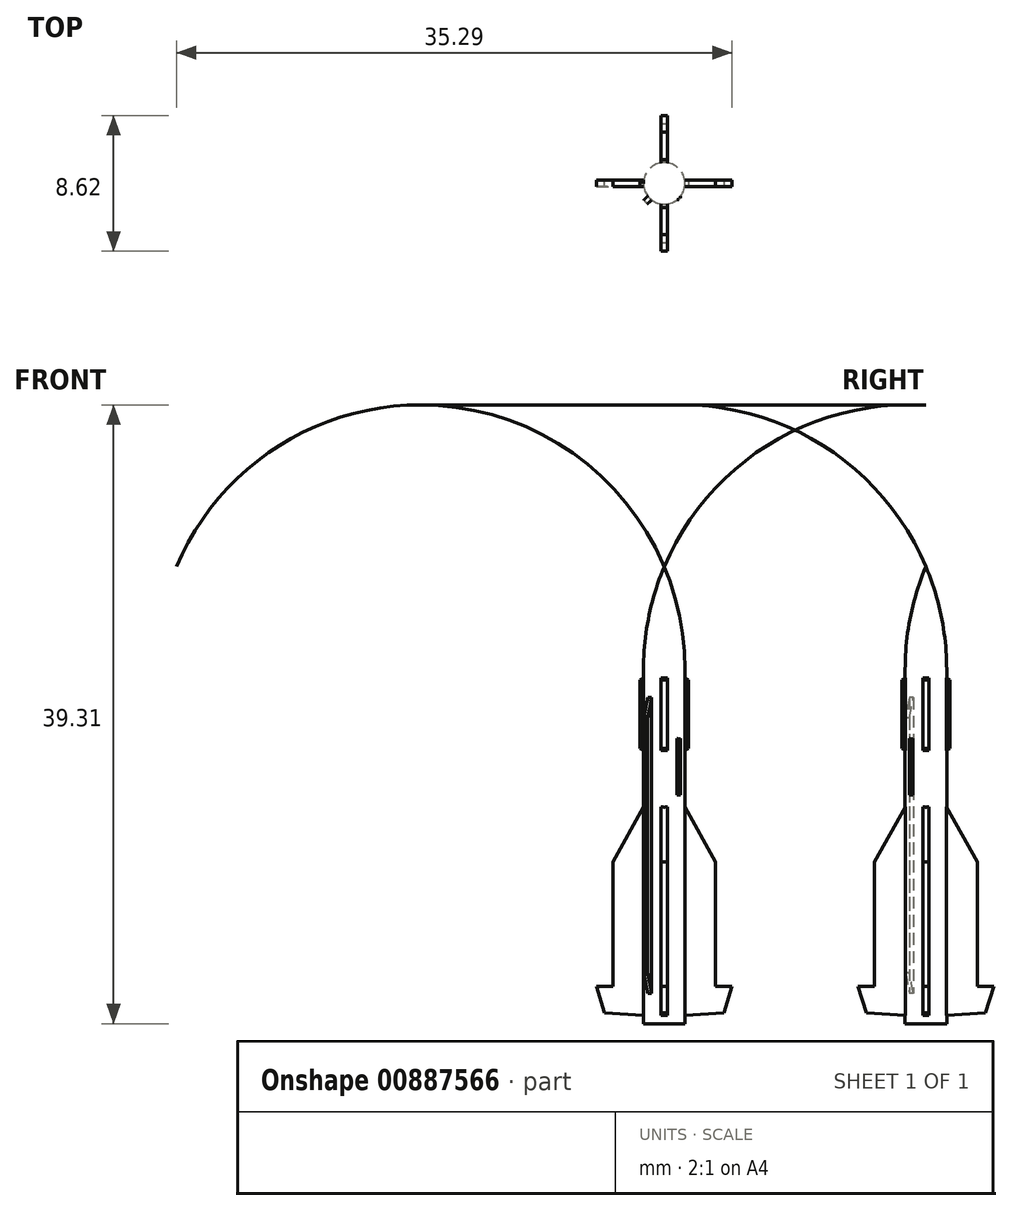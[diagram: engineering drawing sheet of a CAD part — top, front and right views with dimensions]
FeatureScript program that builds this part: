
annotation { "Feature Type Name" : "Feature", "Feature Type Description" : "" }
export const myFeature = defineFeature(function(context is Context, id is Id, definition is map)
    precondition{}
    {
        {
            assignVariable(context, id + "F0", {"name" : "Scale", "anyValue" : 144});
        }
        {
            var Q0;
            Q0=qCreatedBy(makeId("Front.planeOp"),FACE);
            var sketch = newSketch(context, id + "F1", { "sketchPlane" : qUnion([Q0])});
            skLineSegment(sketch, "E0", {"start": v(0, 0) * mm, "end": v(0, 29.03) * mm});
            skLineSegment(sketch, "E1", {"start": v(1.32, 22.5) * mm, "end": v(1.32, 0) * mm});
            skLineSegment(sketch, "E2", {"start": v(1.32, 0) * mm, "end": v(0, 0) * mm});
            skArc(sketch, "E3", {"start": v(1.32, 22.5) * mm, "mid": v(0.99, 25.83) * mm, "end": v(0, 29.03) * mm});
            skSolve(sketch);
        }
        {
            var Q0;
            Q0=makeQuery(id+"F1.imprint","IMPRINT",FACE,{"disambiguationData":[TD([[makeQuery(id+"F1.imprint","IMPRINT",EDGE,{"derivedFrom":sQuery(id+"F1.wireOp",EDGE,"E0")}),-1.0]])]});
            var Q1;
            Q1=sQuery(id+"F1.wireOp",EDGE,"E0");
            revolve(context, id + "F2", {"surfaceOperationType" : NewSurfaceOperationType.NEW, "entities" : qUnion([Q0]), "axis" : qUnion([Q1]), "revolveType" : RevolveType.FULL});
        }
        {
            var Q0;
            Q0=qCreatedBy(makeId("Front.planeOp"),FACE);
            var sketch = newSketch(context, id + "F3", { "sketchPlane" : qUnion([Q0])});
            skLineSegment(sketch, "E4.0", {"start": v(1.32, 22.5) * mm, "end": v(-1.32, 22.5) * mm, "construction": true});
            skLineSegment(sketch, "E5", {"start": v(0, 0.43) * mm, "end": v(3.78, 0.7) * mm});
            skLineSegment(sketch, "E6", {"start": v(4.3, 2.36) * mm, "end": v(1.32, 2.36) * mm});
            skLineSegment(sketch, "E7", {"start": v(0.4, 2.36) * mm, "end": v(0.4, 2.47) * mm});
            skLineSegment(sketch, "E8", {"start": v(0.4, 2.47) * mm, "end": v(3.26, 2.47) * mm});
            skLineSegment(sketch, "E9", {"start": v(0, 22.7) * mm, "end": v(0, 0.43) * mm});
            skLineSegment(sketch, "E10", {"start": v(1.32, 22.5) * mm, "end": v(1.32, 0) * mm, "construction": true});
            skLineSegment(sketch, "E11", {"start": v(1.32, 2.36) * mm, "end": v(0.4, 2.36) * mm});
            skLineSegment(sketch, "E12", {"start": v(3.78, 0.7) * mm, "end": v(4.3, 2.36) * mm});
            skLineSegment(sketch, "E13", {"start": v(3.26, 2.47) * mm, "end": v(3.26, 10.28) * mm});
            skLineSegment(sketch, "E14", {"start": v(0.4, 15.4) * mm, "end": v(0.4, 16.83) * mm});
            skLineSegment(sketch, "E15", {"start": v(1.53, 17.48) * mm, "end": v(0.4, 16.83) * mm});
            skLineSegment(sketch, "E16", {"start": v(1.53, 17.48) * mm, "end": v(1.53, 21.82) * mm});
            skLineSegment(sketch, "E17", {"start": v(1.53, 21.82) * mm, "end": v(0, 22.7) * mm});
            skLineSegment(sketch, "E18", {"start": v(3.26, 10.28) * mm, "end": v(0.4, 15.4) * mm});
            skPoint(sketch, "E19", {"position": v(1.32, 13.75) * mm});
            skPoint(sketch, "E20", {"position": v(1.32, 17.36) * mm});
            skPoint(sketch, "E21", {"position": v(1.32, 21.94) * mm});
            skPoint(sketch, "E22", {"position": v(1.32, 0.52) * mm});
            skLineSegment(sketch, "E23", {"start": v(3.26, 2.47) * mm, "end": v(3.26, 2.36) * mm});
            skSolve(sketch);
        }
        {
            var Q0;
            Q0=qSketchRegion(id+"F3",true);
            extrude(context, id + "F4", {"entities" : qUnion([Q0]), "operationType" : NewBodyOperationType.ADD, "oppositeDirection" : true, "depth" : .4 * mm, "offsetDistance" : 25 * mm, "symmetric" : true});
        }
        {
            var Q0;
            Q0=makeQuery(id+"F2.opRevolve","SWEPT_BODY",BODY,{"disambiguationData":[OSD([sQuery(id+"F1.wireOp",EDGE,"E0"),sQuery(id+"F1.wireOp",EDGE,"E1"),sQuery(id+"F1.wireOp",EDGE,"E2"),sQuery(id+"F1.wireOp",EDGE,"h1jDSi8t-veb7-85qg-XgDk-6E8DmZjBuz4r")])]});
            var Q1;
            Q1=makeQuery(id+"F2.opRevolve","SWEPT_FACE",FACE,{"disambiguationData":[OSD([sQuery(id+"F1.wireOp",EDGE,"E1")])]});
            circularPattern(context, id + "F5", {"operationType" : NewBodyOperationType.ADD, "entities" : qUnion([Q0]), "axis" : qUnion([Q1]), "angle" : 360 * degree, "instanceCount" : 4, "equalSpace" : true, "computeTransformsWithoutBuiltin" : true});
        }
        {
            var Q0;
            Q0=qCreatedBy(makeId("Top.planeOp"),FACE);
            cPlane(context, id + "F6", {"entities" : qUnion([Q0]), "cplaneType" : CPlaneType.OFFSET, "offset" : (465 / 144) * mm, "width" : 150 * mm, "height" : 150 * mm});
        }
        {
            var Q0;
            Q0=qCreatedBy(id+"F6.planeOp",FACE);
            var sketch = newSketch(context, id + "F7", { "sketchPlane" : qUnion([Q0])});
            skLineSegment(sketch, "E24", {"start": v(-1.3, -1.06) * mm, "end": v(-0.86, -0.61) * mm});
            skLineSegment(sketch, "E25", {"start": v(-0.86, -0.61) * mm, "end": v(-0.61, -0.86) * mm});
            skLineSegment(sketch, "E26", {"start": v(-0.61, -0.86) * mm, "end": v(-1.06, -1.3) * mm});
            skLineSegment(sketch, "E27", {"start": v(-0.73, -0.73) * mm, "end": v(0, 0) * mm, "construction": true});
            skLineSegment(sketch, "E28", {"start": v(0, 0) * mm, "end": v(-0.48, 0) * mm, "construction": true});
            skLineSegment(sketch, "E29", {"start": v(-1.3, -1.06) * mm, "end": v(-1.06, -1.3) * mm});
            skCircle(sketch, "E30.0", {"center": v(0, 0) * mm, "radius": 1.32 * mm});
            skSolve(sketch);
        }
        {
            var Q0;
            Q0=makeQuery(id+"F7.imprint","IMPRINT",FACE,{"disambiguationData":[TD([[makeQuery(id+"F7.imprint","IMPRINT",EDGE,{"derivedFrom":sQuery(id+"F7.wireOp",EDGE,"E24")}),-1.0]])]});
            extrude(context, id + "F8", {"entities" : qUnion([Q0]), "operationType" : NewBodyOperationType.ADD, "depth" : (2330 / getVariable(context, 'Scale')) * mm, "offsetDistance" : 25 * mm});
        }
        {
            var Q0;
            Q0=qCreatedBy(makeId("Top.planeOp"),FACE);
            cPlane(context, id + "F9", {"entities" : qUnion([Q0]), "cplaneType" : CPlaneType.OFFSET, "offset" : (2090 / getVariable(context, 'Scale')) * mm, "width" : 150 * mm, "height" : 150 * mm});
        }
        {
            var Q0;
            Q0=qCreatedBy(id+"F9.planeOp",FACE);
            var sketch = newSketch(context, id + "F10", { "sketchPlane" : qUnion([Q0])});
            skLineSegment(sketch, "E31", {"start": v(-0.04, -0.2) * mm, "end": v(0.2, 0.04) * mm});
            skLineSegment(sketch, "E32", {"start": v(0.2, 0.04) * mm, "end": v(1.1, -0.86) * mm});
            skLineSegment(sketch, "E33", {"start": v(0.86, -1.1) * mm, "end": v(-0.04, -0.2) * mm});
            skLineSegment(sketch, "E34", {"start": v(0, -0.5) * mm, "end": v(0, 0) * mm, "construction": true});
            skLineSegment(sketch, "E35", {"start": v(0, 0) * mm, "end": v(0.08, -0.08) * mm, "construction": true});
            skLineSegment(sketch, "E36", {"start": v(0.86, -1.1) * mm, "end": v(1.1, -0.86) * mm});
            skSolve(sketch);
        }
        {
            var Q0;
            Q0=qSketchRegion(id+"F10",true);
            extrude(context, id + "F11", {"entities" : qUnion([Q0]), "operationType" : NewBodyOperationType.ADD, "depth" : (520 / getVariable(context, 'Scale')) * mm, "offsetDistance" : 25 * mm});
        }
        {
            var Q0;
            Q0=makeQuery(id+"F8.boolean.opBoolean","INTERSECT",EDGE,{"derivedFrom":[makeQuery(id+"F2.opRevolve","SWEPT_FACE",FACE,{"disambiguationData":[OSD([sQuery(id+"F1.wireOp",EDGE,"E1")])]}),makeQuery(id+"F8.opExtrude","CAP_FACE",FACE,{"disambiguationData":[OSD([sQuery(id+"F7.wireOp",EDGE,"E24"),sQuery(id+"F7.wireOp",EDGE,"E25"),sQuery(id+"F7.wireOp",EDGE,"E26"),sQuery(id+"F7.wireOp",EDGE,"wgWcNRNm-otso-AYOS-fXFW-FSscdqUkpizS")])],"isStart":false})]});
            var Q1;
            Q1=makeQuery(id+"F8.boolean.opBoolean","INTERSECT",EDGE,{"derivedFrom":[makeQuery(id+"F2.opRevolve","SWEPT_FACE",FACE,{"disambiguationData":[OSD([sQuery(id+"F1.wireOp",EDGE,"E1")])]}),makeQuery(id+"F8.opExtrude","CAP_FACE",FACE,{"disambiguationData":[OSD([sQuery(id+"F7.wireOp",EDGE,"E24"),sQuery(id+"F7.wireOp",EDGE,"E25"),sQuery(id+"F7.wireOp",EDGE,"E26"),sQuery(id+"F7.wireOp",EDGE,"wgWcNRNm-otso-AYOS-fXFW-FSscdqUkpizS")])],"isStart":true})]});
            chamfer(context, id + "F12", {"entities" : qUnion([Q0, Q1]), "chamferType" : ChamferType.OFFSET_ANGLE, "width" : (50 / getVariable(context, 'Scale')) * mm, "oppositeDirection" : true, "angle" : 75 * degree, "tangentPropagation" : true});
        }
        {
            var Q0;
            Q0=makeQuery(id+"F11.opExtrude","SWEPT_FACE",FACE,{"disambiguationData":[OSD([sQuery(id+"F10.wireOp",EDGE,"E36")])]});
            chamfer(context, id + "F13", {"entities" : qUnion([Q0]), "width" : .1 * mm, "tangentPropagation" : true});
        }
    });
